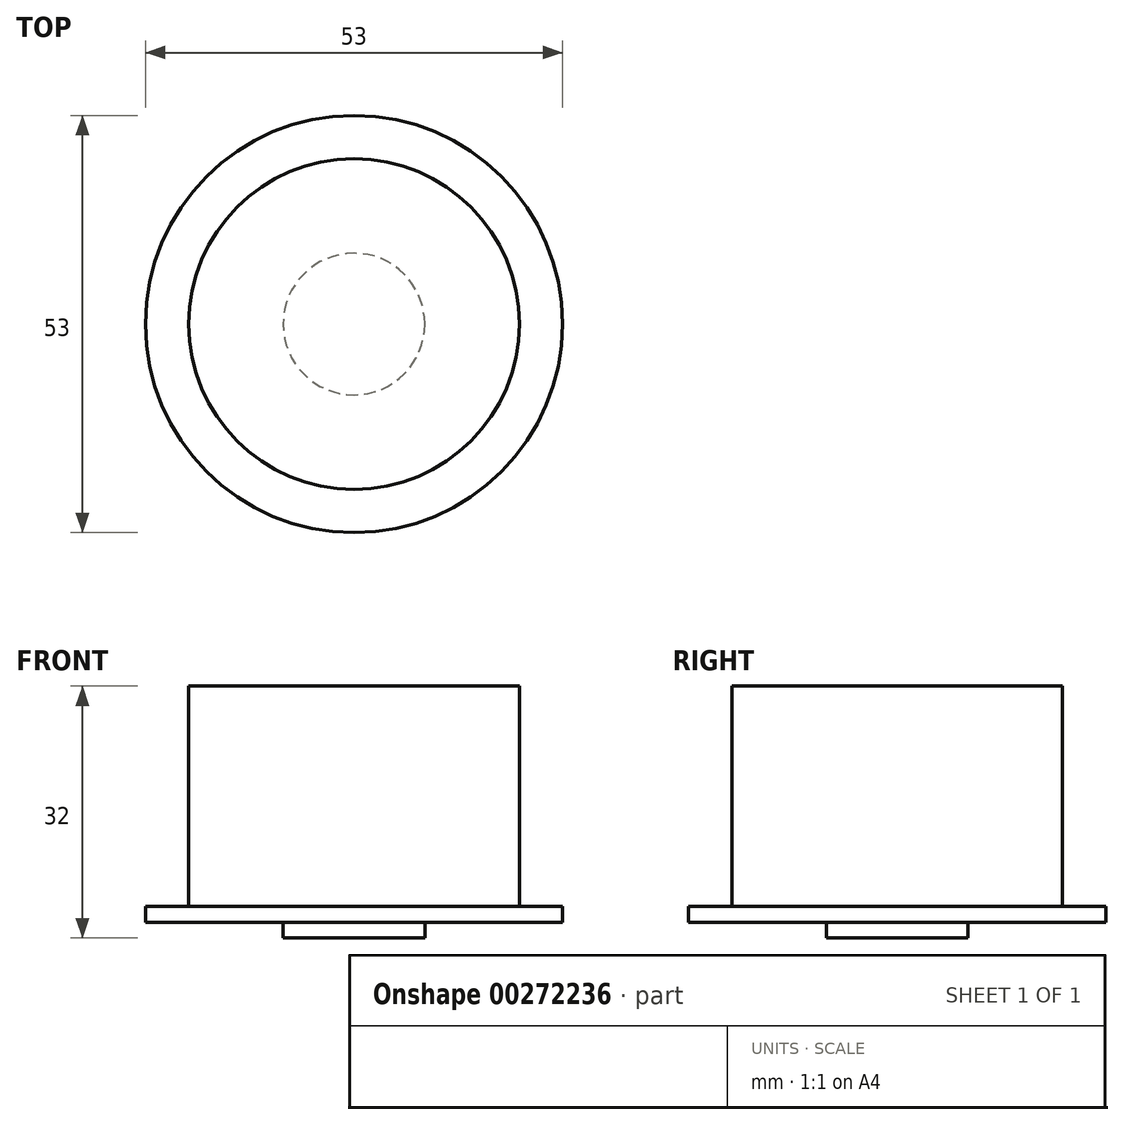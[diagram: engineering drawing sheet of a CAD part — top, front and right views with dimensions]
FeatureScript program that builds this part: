
annotation { "Feature Type Name" : "Feature", "Feature Type Description" : "" }
export const myFeature = defineFeature(function(context is Context, id is Id, definition is map)
    precondition{}
    {
        {
            var Q0;
            Q0=qCreatedBy(makeId("Top.planeOp"),FACE);
            var sketch = newSketch(context, id + "F0", { "sketchPlane" : qUnion([Q0])});
            skCircle(sketch, "E0", {"center": v(0, 0) * mm, "radius": 26.5 * mm});
            skSolve(sketch);
        }
        {
            var Q0;
            Q0=makeQuery(id+"F0.imprint","IMPRINT",FACE,{"disambiguationData":[TD([[makeQuery(id+"F0.imprint","IMPRINT",EDGE,{"derivedFrom":sQuery(id+"F0.wireOp",EDGE,"E0")}),1.0]])]});
            extrude(context, id + "F1", {"entities" : qUnion([Q0]), "depth" : 2 * mm});
        }
        {
            var Q0;
            Q0=makeQuery(id+"F1.opExtrude","CAP_FACE",FACE,{"disambiguationData":[OSD([sQuery(id+"F0.wireOp",EDGE,"E0")])],"isStart":true});
            var sketch = newSketch(context, id + "F2", { "sketchPlane" : qUnion([Q0])});
            skCircle(sketch, "E1", {"center": v(0, 0) * mm, "radius": 9 * mm});
            skSolve(sketch);
        }
        {
            var Q0;
            Q0=makeQuery(id+"F2.imprint","IMPRINT",FACE,{"disambiguationData":[TD([[makeQuery(id+"F2.imprint","IMPRINT",EDGE,{"derivedFrom":sQuery(id+"F2.wireOp",EDGE,"E1")}),1.0]])]});
            extrude(context, id + "F3", {"entities" : qUnion([Q0]), "operationType" : NewBodyOperationType.ADD, "depth" : 2 * mm});
        }
        {
            var Q0;
            Q0=makeQuery(id+"F1.opExtrude","CAP_FACE",FACE,{"disambiguationData":[OSD([sQuery(id+"F0.wireOp",EDGE,"E0")])],"isStart":false});
            var sketch = newSketch(context, id + "F4", { "sketchPlane" : qUnion([Q0])});
            skCircle(sketch, "E2", {"center": v(0, 0) * mm, "radius": 21 * mm});
            skSolve(sketch);
        }
        {
            var Q0;
            Q0=makeQuery(id+"F4.imprint","IMPRINT",FACE,{"disambiguationData":[TD([[makeQuery(id+"F4.imprint","IMPRINT",EDGE,{"derivedFrom":sQuery(id+"F4.wireOp",EDGE,"E2")}),1.0]])]});
            extrude(context, id + "F5", {"entities" : qUnion([Q0]), "operationType" : NewBodyOperationType.ADD, "depth" : 28 * mm});
        }
    });
